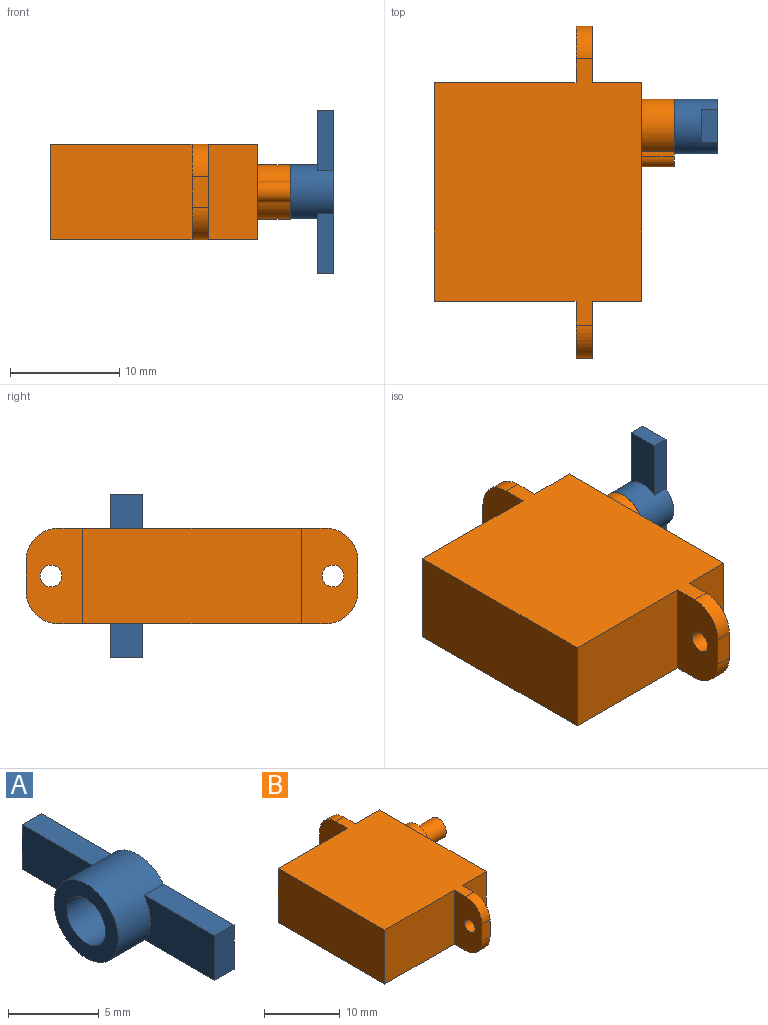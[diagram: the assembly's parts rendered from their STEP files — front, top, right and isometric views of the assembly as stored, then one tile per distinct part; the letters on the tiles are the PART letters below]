
ASSEMBLY  parts=2 mates=1
PART A: 12 faces, bbox 4x15x5 mm
  f0: cylinder r=2.5mm len=5mm, axis (-1,0,0), area 53.2mm2, adj f1,f2,f4,f5,f6,f7,f8,f9
  f1: plane 15x5mm, normal (1,0,0), area 43.5mm2, adj f0,f3,f5,f6,f8,f9,f10,f11
  f2: plane 5x5mm, normal (-1,0,0), area 12.6mm2, adj f0,f11
  f3: plane 3x1.5mm, normal (0,-1,0), area 4.5mm2, adj f1,f4,f5,f6
  f4: plane 5.5x3mm, normal (-1,0,0), area 15.5mm2, adj f0,f3,f5,f6
  f5: plane 5.5x1.5mm, normal (0,0,1), area 8.2mm2, adj f0,f1,f3,f4
  f6: plane 5.5x1.5mm, normal (0,0,-1), area 8.2mm2, adj f0,f1,f3,f4
  f7: plane 5.5x3mm, normal (-1,0,0), area 15.5mm2, adj f0,f8,f9,f10
  f8: plane 5.5x1.5mm, normal (0,0,-1), area 8.2mm2, adj f0,f1,f7,f10
  f9: plane 5.5x1.5mm, normal (0,0,1), area 8.2mm2, adj f0,f1,f7,f10
  f10: plane 3x1.5mm, normal (0,1,0), area 4.5mm2, adj f1,f7,f8,f9
  f11: cylinder r=1.5mm len=4mm, axis (1,0,0), area 37.7mm2, adj f1,f2
PART B: 27 faces, bbox 26x30.4x8.8 mm
  f0: plane 13x8.75mm, normal (0,-1,0), area 113.8mm2, adj f2,f6,f7,f13
  f1: plane 13x8.75mm, normal (0,1,0), area 113.8mm2, adj f2,f6,f7,f11
  f2: plane 20x8.75mm, normal (-1,0,0), area 175mm2, adj f0,f1,f6,f7
  f3: plane 8.75x4.5mm, normal (0,-1,0), area 39.4mm2, adj f4,f6,f7,f12
  f4: plane 20x8.75mm, normal (1,0,0), area 153.3mm2, adj f3,f5,f6,f7,f16,f17,f18,f19
  f5: plane 8.75x4.5mm, normal (0,1,0), area 39.4mm2, adj f4,f6,f7,f10
  f6: plane 24.39x19mm, normal (0,0,1), area 386.6mm2, adj f0,f1,f2,f3,f4,f5,f10,f11
  f7: plane 24.39x19mm, normal (0,0,-1), area 386.6mm2, adj f0,f1,f2,f3,f4,f5,f10,f11
  f8: cylinder r=1mm len=2mm, axis (-1,0,0), area 9.4mm2, adj f10,f11
  f9: plane 2.75x1.5mm, normal (0,1,0), area 4.1mm2, adj f10,f11,f23,f24
  f10: plane 8.75x5.2mm, normal (1,0,0), area 38.5mm2, adj f5,f6,f7,f8,f9,f23,f24
  f11: plane 8.75x5.2mm, normal (-1,0,0), area 38.5mm2, adj f1,f6,f7,f8,f9,f23,f24
  f12: plane 8.75x5.2mm, normal (1,0,0), area 38.5mm2, adj f3,f6,f7,f14,f15,f25,f26
  f13: plane 8.75x5.2mm, normal (-1,0,0), area 38.5mm2, adj f0,f6,f7,f14,f15,f25,f26
  f14: cylinder r=1mm len=2mm, axis (-1,0,0), area 9.4mm2, adj f12,f13
  f15: plane 2.75x1.5mm, normal (0,-1,0), area 4.1mm2, adj f12,f13,f25,f26
  f16: cylinder r=2.5mm len=5mm, axis (-1,0,0), area 41mm2, adj f4,f17,f19,f20
  f17: plane 3x0.41mm, normal (0,0,1), area 1.2mm2, adj f4,f16,f18,f20
  f18: cylinder r=0.99mm len=3mm, axis (-1,0,0), area 9.3mm2, adj f4,f17,f19,f20
  f19: plane 3x0.41mm, normal (0,0,-1), area 1.2mm2, adj f4,f16,f18,f20
  f20: plane 6.2x5mm, normal (1,0,0), area 14.6mm2, adj f16,f17,f18,f19,f21
  f21: cylinder r=1.5mm len=4mm, axis (-1,0,0), area 37.7mm2, adj f20,f22
  f22: plane 3x3mm, normal (1,0,0), area 7.1mm2, adj f21
  f23: cylinder r=3mm len=3mm, axis (1,0,0), area 7.1mm2, adj f7,f9,f10,f11
  f24: cylinder r=3mm len=3mm, axis (-1,0,0), area 7.1mm2, adj f6,f9,f10,f11
  f25: cylinder r=3mm len=3mm, axis (1,0,0), area 7.1mm2, adj f6,f12,f13,f15
  f26: cylinder r=3mm len=3mm, axis (-1,0,0), area 7.1mm2, adj f7,f12,f13,f15
PLACE A rot(axis=(-1,0,0),90deg) t=(3,6,0)mm
PLACE B at identity fixed
MATE fastened B.f16 <-> A.f0  axis (1,0,0) through (7,6,0)mm
